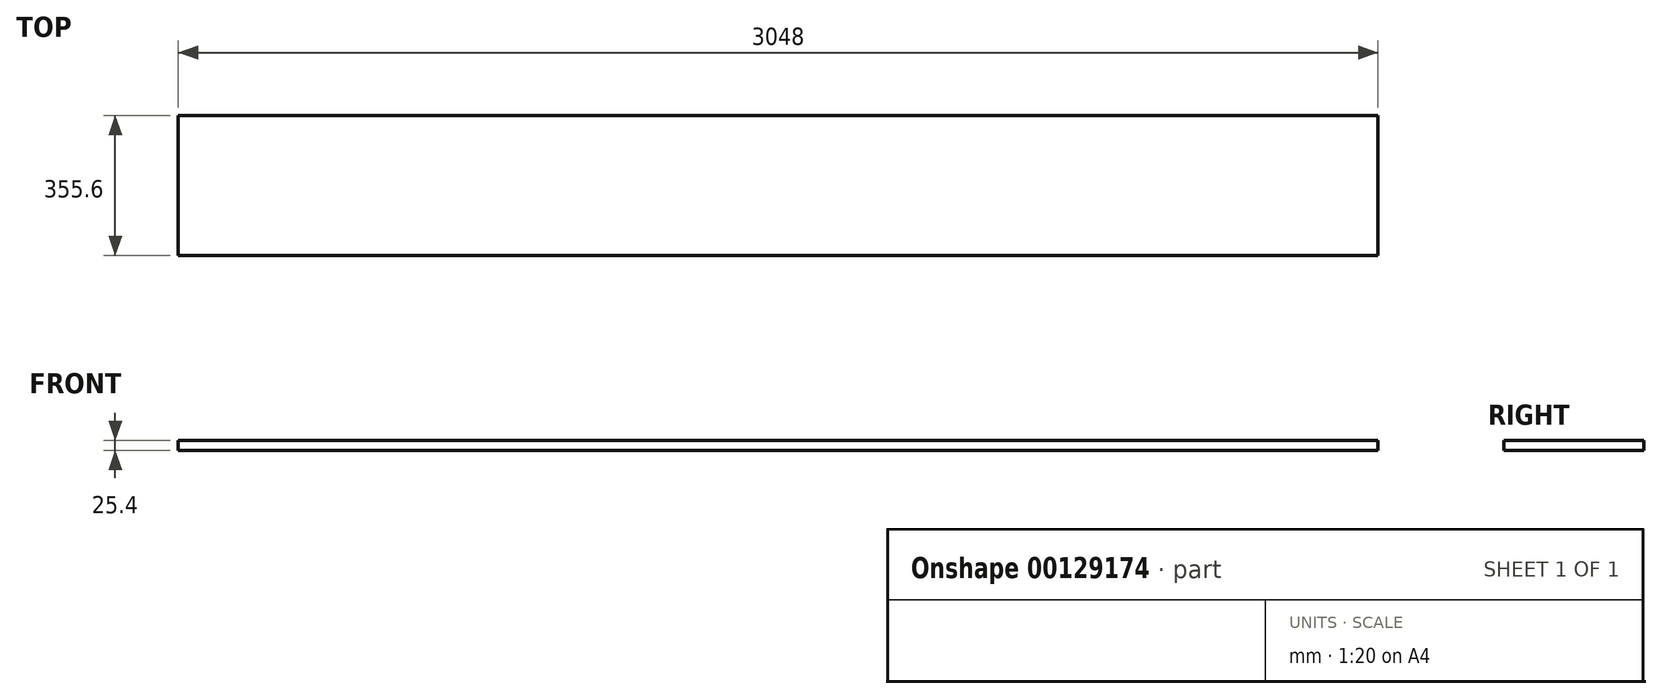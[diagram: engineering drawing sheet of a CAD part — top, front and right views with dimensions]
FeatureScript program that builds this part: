
annotation { "Feature Type Name" : "Feature", "Feature Type Description" : "" }
export const myFeature = defineFeature(function(context is Context, id is Id, definition is map)
    precondition{}
    {
        {
            var Q0;
            Q0=qCreatedBy(makeId("Top.planeOp"),FACE);
            var sketch = newSketch(context, id + "F0", { "sketchPlane" : qUnion([Q0])});
            skLineSegment(sketch, "E0.bottom", {"start": v(1524, 177.8) * mm, "end": v(-1524, 177.8) * mm});
            skLineSegment(sketch, "E0.top", {"start": v(1524, -177.8) * mm, "end": v(-1524, -177.8) * mm});
            skLineSegment(sketch, "E0.left", {"start": v(1524, 177.8) * mm, "end": v(1524, -177.8) * mm});
            skLineSegment(sketch, "E0.right", {"start": v(-1524, 177.8) * mm, "end": v(-1524, -177.8) * mm});
            skPoint(sketch, "E0.middle", {"position": v(0, 0) * mm});
            skSolve(sketch);
        }
        {
            var Q0;
            Q0 = qSketchRegion(id + "F0", true);
            extrude(context, id + "F1", {"entities" : qUnion([Q0]), "depth" : 25.4 * mm});
        }
    });
